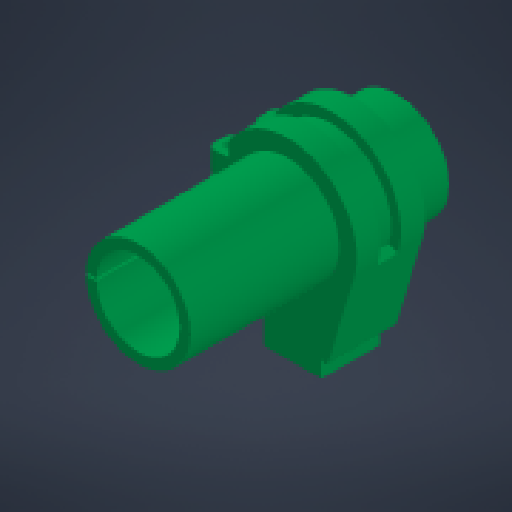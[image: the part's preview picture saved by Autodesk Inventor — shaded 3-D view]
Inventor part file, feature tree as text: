
AUTODESK INVENTOR PART (.ipt)
format: ipt  version: 2024 (Build 280153000, 153)  size: 461,312 bytes
history: native  units: mm
features: other x16, sketch x15, extrude x12, fillet x4, mirror x3, projected_geometry x3, reference x2, shell x1, sweep x1
ambient origin geometry x8: Origin, YZ Plane, XZ Plane, XY Plane, X Axis, Y Axis, Z Axis, Center Point
bodies: Body1 (feature_tree)
feature tree (57):
  other  "Твердое тело1"
  extrude  "Выдавливание1"  Depth=20.0mm
  shell  "Оболочка1"  Thickness=1.5mm
  extrude  "Выдавливание2"  Depth=20.0mm TaperAngle=0.0deg
  other  "РабПлоскость1"
  extrude  "Выдавливание4"  Depth=4.0mm
  sketch  "Эскиз8"
  other  "РабПлоскость3"
  sweep  "Сдвиг1"
  other  "РабОсь1"
  other  "РабПлоскость4"
  fillet  "Сопряжение2"  Radius=5.0mm
  other  "РабПлоскость5"
  other  "РабПлоскость6"
  other  "РабПлоскость7"
  other  "РабПлоскость8"
  extrude  "Выдавливание18"  Depth=20.0mm TaperAngle=0.0deg
  extrude  "Выдавливание19"  Depth=20.2mm
  extrude  "Выдавливание20"  Depth=24.4mm
  mirror  "Зеркальное отражение7"
  other  "Непосредственное редактирование3"
  fillet  "Сопряжение9"  Radius=8.0mm
  fillet  "Сопряжение10"  [1 undecoded]
  other  "Непосредственное редактирование4"
  extrude  "Выдавливание22"  Depth=3.0mm
  mirror  "Зеркальное отражение8"
  extrude  "Выдавливание23"  Depth=6.0mm
  extrude  "Выдавливание24"  Depth=1.0mm
  extrude  "Выдавливание25"  Depth=6.0mm
  mirror  "Зеркальное отражение9"
  extrude  "Выдавливание26"  Depth=16.25mm TaperAngle=0.0deg
  fillet  "Сопряжение11"  Radius=3.0mm
  extrude  "Выдавливание27"  Depth=18.5mm TaperAngle=0.0deg
  sketch  "Эскиз1"
  sketch  "Эскиз2"
  projected_geometry  "Спроецированная петля1"
  sketch  "Эскиз5"
  reference  "Ссылка3"
  reference  "Ссылка4"
  sketch  "Эскиз10"
  sketch  "3D эскиз1"
  sketch  "Эскиз32"
  sketch  "Эскиз33"
  sketch  "Эскиз35"
  sketch  "Эскиз37"
  sketch  "Эскиз39"
  sketch  "Эскиз40"
  projected_geometry  "Спроецированная петля3"
  sketch  "Эскиз41"
  sketch  "Эскиз42"
  sketch  "Эскиз43"
  projected_geometry  "Спроецированная петля4"
  parser-record x1  (decoder bookkeeping rows leaked as tree rows — omitted from the tree; the rows remain in map.json)
  other  "arm_assembly.iam"
  other  "arm:1"
  other  "Перенос3"
  other  "Перенос4"
note: 1 required parameter value undecoded (feature->parameter linkage not recoverable at this tier; creation-order binding heuristic only, values carry confidence <= 0.55)
note: 1 file-system path scrubbed to <path> (originals preserved in map.json)
